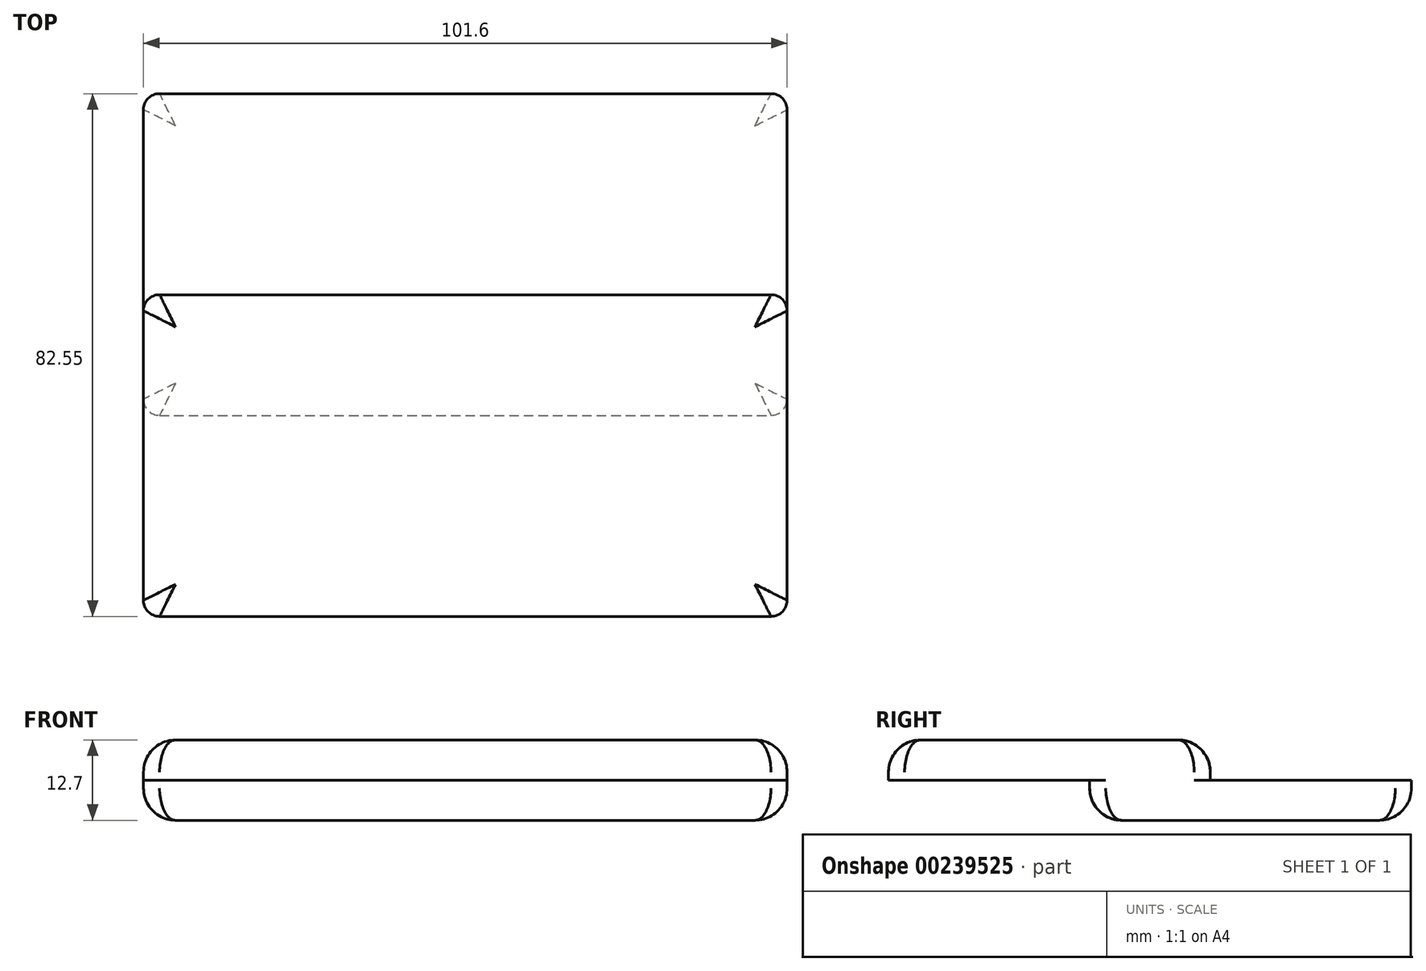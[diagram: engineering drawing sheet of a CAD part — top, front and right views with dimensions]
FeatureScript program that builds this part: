
annotation { "Feature Type Name" : "Feature", "Feature Type Description" : "" }
export const myFeature = defineFeature(function(context is Context, id is Id, definition is map)
    precondition{}
    {
        {
            var Q0;
            Q0=qCreatedBy(makeId("Top.planeOp"),FACE);
            var sketch = newSketch(context, id + "F0", { "sketchPlane" : qUnion([Q0])});
            skLineSegment(sketch, "E0.bottom", {"start": v(-50.8, 25.4) * mm, "end": v(50.8, 25.4) * mm});
            skLineSegment(sketch, "E0.top", {"start": v(-50.8, -25.4) * mm, "end": v(50.8, -25.4) * mm});
            skLineSegment(sketch, "E0.left", {"start": v(-50.8, 25.4) * mm, "end": v(-50.8, -25.4) * mm});
            skLineSegment(sketch, "E0.right", {"start": v(50.8, 25.4) * mm, "end": v(50.8, -25.4) * mm});
            skPoint(sketch, "E0.middle", {"position": v(0, 0) * mm});
            skSolve(sketch);
        }
        {
            var Q0;
            Q0 = qSketchRegion(id + "F0", true);
            extrude(context, id + "F1", {"entities" : qUnion([Q0]), "endBound" : BoundingType.SYMMETRIC, "depth" : 6.35 * mm});
        }
        {
            var Q0;
            Q0=makeQuery(id+"F1.opExtrude","CAP_FACE",FACE,{"disambiguationData":[OSD([sQuery(id+"F0.wireOp",EDGE,"E0.bottom"),sQuery(id+"F0.wireOp",EDGE,"E0.top"),sQuery(id+"F0.wireOp",EDGE,"E0.left"),sQuery(id+"F0.wireOp",EDGE,"E0.right")])],"isStart":false});
            var sketch = newSketch(context, id + "F2", { "sketchPlane" : qUnion([Q0])});
            skLineSegment(sketch, "E1.bottom", {"start": v(-50.8, -25.4) * mm, "end": v(50.8, -25.4) * mm});
            skLineSegment(sketch, "E1.top", {"start": v(-50.8, -6.35) * mm, "end": v(50.8, -6.35) * mm});
            skLineSegment(sketch, "E1.left", {"start": v(-50.8, -25.4) * mm, "end": v(-50.8, -6.35) * mm});
            skLineSegment(sketch, "E1.right", {"start": v(50.8, -25.4) * mm, "end": v(50.8, -6.35) * mm});
            skSolve(sketch);
        }
        {
            var Q0;
            Q0 = qSketchRegion(id + "F2", true);
            extrude(context, id + "F3", {"entities" : qUnion([Q0]), "operationType" : NewBodyOperationType.ADD, "depth" : 6.35 * mm});
        }
        {
            var Q0;
            Q0=makeQuery(id+"F3.boolean.opBoolean","MERGE",FACE,{"derivedFrom":[makeQuery(id+"F1.opExtrude","SWEPT_FACE",FACE,{"disambiguationData":[OSD([sQuery(id+"F0.wireOp",EDGE,"E0.top")])]}),makeQuery(id+"F3.opExtrude","SWEPT_FACE",FACE,{"disambiguationData":[OSD([sQuery(id+"F2.wireOp",EDGE,"E1.bottom")])]})]});
            var sketch = newSketch(context, id + "F4", { "sketchPlane" : qUnion([Q0])});
            skLineSegment(sketch, "E2.bottom", {"start": v(-50.8, 9.53) * mm, "end": v(50.8, 9.53) * mm});
            skLineSegment(sketch, "E2.top", {"start": v(-50.8, 3.17) * mm, "end": v(50.8, 3.17) * mm});
            skLineSegment(sketch, "E2.left", {"start": v(-50.8, 9.53) * mm, "end": v(-50.8, 3.17) * mm});
            skLineSegment(sketch, "E2.right", {"start": v(50.8, 9.53) * mm, "end": v(50.8, 3.17) * mm});
            skSolve(sketch);
        }
        {
            var Q0;
            Q0 = qSketchRegion(id + "F4", true);
            extrude(context, id + "F5", {"entities" : qUnion([Q0]), "operationType" : NewBodyOperationType.ADD, "depth" : 31.75 * mm});
        }
        {
            var Q0;
            Q0=makeQuery(id+"F5.boolean.opBoolean","MERGE",EDGE,{"derivedFrom":[makeQuery(id+"F3.opExtrude","CAP_EDGE",EDGE,{"disambiguationData":[OSD([sQuery(id+"F2.wireOp",EDGE,"E1.left")])],"isStart":false}),makeQuery(id+"F5.opExtrude","SWEPT_EDGE",EDGE,{"disambiguationData":[OSD([sQuery(id+"F4.wireOp",EDGE,"E2.bottom"),sQuery(id+"F4.wireOp",EDGE,"E2.left")])]})]});
            var Q1;
            Q1=makeQuery(id+"F1.opExtrude","CAP_EDGE",EDGE,{"disambiguationData":[OSD([sQuery(id+"F0.wireOp",EDGE,"E0.left")])],"isStart":true});
            var Q2;
            Q2=makeQuery(id+"F5.opExtrude","CAP_EDGE",EDGE,{"disambiguationData":[OSD([sQuery(id+"F4.wireOp",EDGE,"E2.bottom")])],"isStart":false});
            var Q3;
            Q3=makeQuery(id+"F1.opExtrude","CAP_EDGE",EDGE,{"disambiguationData":[OSD([sQuery(id+"F0.wireOp",EDGE,"E0.top")])],"isStart":true});
            var Q4;
            Q4=makeQuery(id+"F1.opExtrude","CAP_EDGE",EDGE,{"disambiguationData":[OSD([sQuery(id+"F0.wireOp",EDGE,"E0.right")])],"isStart":true});
            var Q5;
            Q5=makeQuery(id+"F5.boolean.opBoolean","MERGE",EDGE,{"derivedFrom":[makeQuery(id+"F3.opExtrude","CAP_EDGE",EDGE,{"disambiguationData":[OSD([sQuery(id+"F2.wireOp",EDGE,"E1.right")])],"isStart":false}),makeQuery(id+"F5.opExtrude","SWEPT_EDGE",EDGE,{"disambiguationData":[OSD([sQuery(id+"F4.wireOp",EDGE,"E2.bottom"),sQuery(id+"F4.wireOp",EDGE,"E2.right")])]})]});
            var Q6;
            Q6=makeQuery(id+"F1.opExtrude","CAP_EDGE",EDGE,{"disambiguationData":[OSD([sQuery(id+"F0.wireOp",EDGE,"E0.bottom")])],"isStart":true});
            var Q7;
            Q7=makeQuery(id+"F3.opExtrude","CAP_EDGE",EDGE,{"disambiguationData":[OSD([sQuery(id+"F2.wireOp",EDGE,"E1.top")])],"isStart":false});
            fillet(context, id + "F6", {"entities" : qUnion([Q0, Q1, Q2, Q3, Q4, Q5, Q6, Q7]), "radius" : 5.08 * mm, "tangentPropagation" : true, "allowEdgeOverflow" : false});
        }
        {
            var Q0;
            {var subQ0=sQuery(id+"F4.wireOp",EDGE,"E2.bottom");Q0=makeQuery(id+"F6.opFillet","BLEND_EDGE",EDGE,{"blendedFrom":[makeQuery(id+"F5.opExtrude","CAP_EDGE",EDGE,{"disambiguationData":[OSD([subQ0])],"isStart":false}),makeQuery(id+"F5.boolean.opBoolean","MERGE",EDGE,{"derivedFrom":[makeQuery(id+"F3.opExtrude","CAP_EDGE",EDGE,{"disambiguationData":[OSD([sQuery(id+"F2.wireOp",EDGE,"E1.right")])],"isStart":false}),makeQuery(id+"F5.opExtrude","SWEPT_EDGE",EDGE,{"disambiguationData":[OSD([subQ0,sQuery(id+"F4.wireOp",EDGE,"E2.right")])]})]})],"blendedInto":[]});}
            var Q1;
            Q1=makeQuery(id+"F6.opFillet","BLEND_EDGE",EDGE,{"blendedFrom":[makeQuery(id+"F3.opExtrude","CAP_EDGE",EDGE,{"disambiguationData":[OSD([sQuery(id+"F2.wireOp",EDGE,"E1.top")])],"isStart":false}),makeQuery(id+"F5.boolean.opBoolean","MERGE",EDGE,{"derivedFrom":[makeQuery(id+"F3.opExtrude","CAP_EDGE",EDGE,{"disambiguationData":[OSD([sQuery(id+"F2.wireOp",EDGE,"E1.right")])],"isStart":false}),makeQuery(id+"F5.opExtrude","SWEPT_EDGE",EDGE,{"disambiguationData":[OSD([sQuery(id+"F4.wireOp",EDGE,"E2.bottom"),sQuery(id+"F4.wireOp",EDGE,"E2.right")])]})]})],"blendedInto":[]});
            var Q2;
            Q2=makeQuery(id+"F6.opFillet","BLEND_EDGE",EDGE,{"blendedFrom":[makeQuery(id+"F3.opExtrude","CAP_EDGE",EDGE,{"disambiguationData":[OSD([sQuery(id+"F2.wireOp",EDGE,"E1.top")])],"isStart":false}),makeQuery(id+"F5.boolean.opBoolean","MERGE",EDGE,{"derivedFrom":[makeQuery(id+"F3.opExtrude","CAP_EDGE",EDGE,{"disambiguationData":[OSD([sQuery(id+"F2.wireOp",EDGE,"E1.left")])],"isStart":false}),makeQuery(id+"F5.opExtrude","SWEPT_EDGE",EDGE,{"disambiguationData":[OSD([sQuery(id+"F4.wireOp",EDGE,"E2.bottom"),sQuery(id+"F4.wireOp",EDGE,"E2.left")])]})]})],"blendedInto":[]});
            var Q3;
            {var subQ0=sQuery(id+"F4.wireOp",EDGE,"E2.bottom");Q3=makeQuery(id+"F6.opFillet","BLEND_EDGE",EDGE,{"blendedFrom":[makeQuery(id+"F5.opExtrude","CAP_EDGE",EDGE,{"disambiguationData":[OSD([subQ0])],"isStart":false}),makeQuery(id+"F5.boolean.opBoolean","MERGE",EDGE,{"derivedFrom":[makeQuery(id+"F3.opExtrude","CAP_EDGE",EDGE,{"disambiguationData":[OSD([sQuery(id+"F2.wireOp",EDGE,"E1.left")])],"isStart":false}),makeQuery(id+"F5.opExtrude","SWEPT_EDGE",EDGE,{"disambiguationData":[OSD([subQ0,sQuery(id+"F4.wireOp",EDGE,"E2.left")])]})]})],"blendedInto":[]});}
            var Q4;
            Q4=makeQuery(id+"F6.opFillet","BLEND_EDGE",EDGE,{"blendedFrom":[makeQuery(id+"F1.opExtrude","CAP_EDGE",EDGE,{"disambiguationData":[OSD([sQuery(id+"F0.wireOp",EDGE,"E0.bottom")])],"isStart":true}),makeQuery(id+"F1.opExtrude","CAP_EDGE",EDGE,{"disambiguationData":[OSD([sQuery(id+"F0.wireOp",EDGE,"E0.right")])],"isStart":true})],"blendedInto":[]});
            var Q5;
            Q5=makeQuery(id+"F6.opFillet","BLEND_EDGE",EDGE,{"blendedFrom":[makeQuery(id+"F1.opExtrude","CAP_EDGE",EDGE,{"disambiguationData":[OSD([sQuery(id+"F0.wireOp",EDGE,"E0.top")])],"isStart":true}),makeQuery(id+"F1.opExtrude","CAP_EDGE",EDGE,{"disambiguationData":[OSD([sQuery(id+"F0.wireOp",EDGE,"E0.right")])],"isStart":true})],"blendedInto":[]});
            var Q6;
            Q6=makeQuery(id+"F6.opFillet","BLEND_EDGE",EDGE,{"blendedFrom":[makeQuery(id+"F1.opExtrude","CAP_EDGE",EDGE,{"disambiguationData":[OSD([sQuery(id+"F0.wireOp",EDGE,"E0.top")])],"isStart":true}),makeQuery(id+"F1.opExtrude","CAP_EDGE",EDGE,{"disambiguationData":[OSD([sQuery(id+"F0.wireOp",EDGE,"E0.left")])],"isStart":true})],"blendedInto":[]});
            var Q7;
            Q7=makeQuery(id+"F6.opFillet","BLEND_EDGE",EDGE,{"blendedFrom":[makeQuery(id+"F1.opExtrude","CAP_EDGE",EDGE,{"disambiguationData":[OSD([sQuery(id+"F0.wireOp",EDGE,"E0.bottom")])],"isStart":true}),makeQuery(id+"F1.opExtrude","CAP_EDGE",EDGE,{"disambiguationData":[OSD([sQuery(id+"F0.wireOp",EDGE,"E0.left")])],"isStart":true})],"blendedInto":[]});
            fillet(context, id + "F7", {"entities" : qUnion([Q0, Q1, Q2, Q3, Q4, Q5, Q6, Q7]), "radius" : 2.54 * mm, "tangentPropagation" : true, "allowEdgeOverflow" : false});
        }
    });
